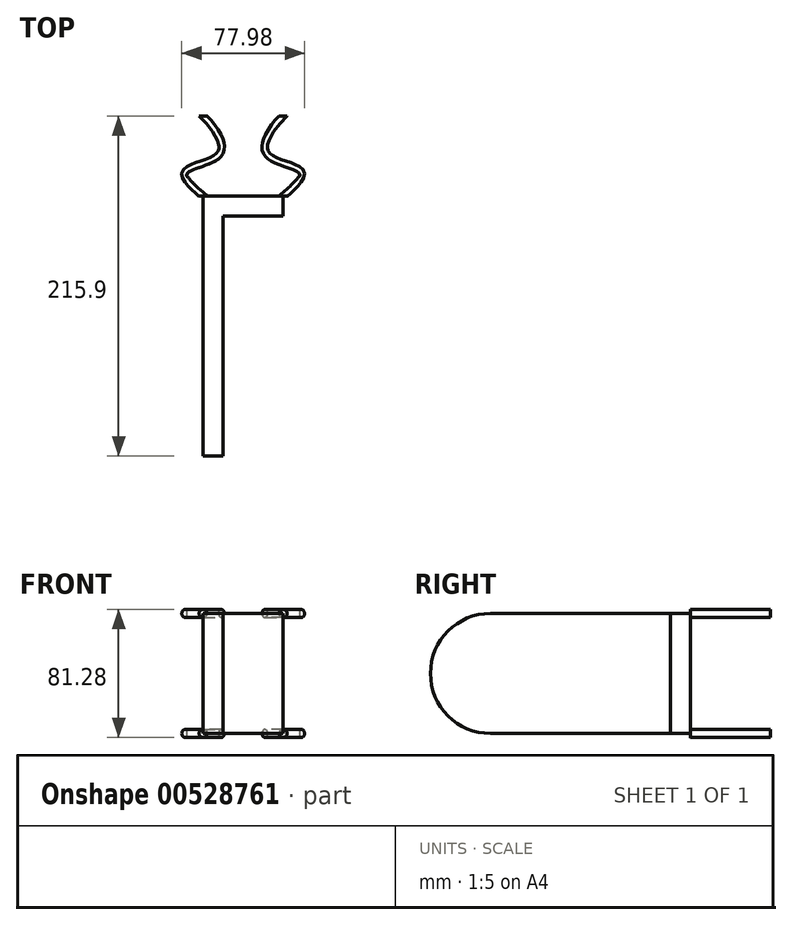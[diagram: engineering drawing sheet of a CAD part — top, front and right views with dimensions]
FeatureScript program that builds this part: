
annotation { "Feature Type Name" : "Feature", "Feature Type Description" : "" }
export const myFeature = defineFeature(function(context is Context, id is Id, definition is map)
    precondition{}
    {
        {
            var Q0;
            Q0=qCreatedBy(makeId("Front.planeOp"),FACE);
            var sketch = newSketch(context, id + "F0", { "sketchPlane" : qUnion([Q0])});
            skLineSegment(sketch, "E0.bottom", {"start": v(-50.8, 76.2) * mm, "end": v(0, 76.2) * mm});
            skLineSegment(sketch, "E0.top", {"start": v(-50.8, 0) * mm, "end": v(0, 0) * mm});
            skLineSegment(sketch, "E0.left", {"start": v(-50.8, 76.2) * mm, "end": v(-50.8, 0) * mm});
            skLineSegment(sketch, "E0.right", {"start": v(0, 76.2) * mm, "end": v(0, 0) * mm});
            skSolve(sketch);
        }
        {
            var Q0;
            Q0=makeQuery(id+"F0.imprint","IMPRINT",FACE,{"disambiguationData":[TD([[makeQuery(id+"F0.imprint","IMPRINT",EDGE,{"derivedFrom":sQuery(id+"F0.wireOp",EDGE,"E0.bottom")}),-1.0]])]});
            extrude(context, id + "F1", {"entities" : qUnion([Q0]), "depth" : 12.7 * mm, "offsetDistance" : 25.4 * mm});
        }
        {
            var Q0;
            Q0=qCreatedBy(makeId("Front.planeOp"),FACE);
            cPlane(context, id + "F2", {"entities" : qUnion([Q0]), "cplaneType" : CPlaneType.OFFSET, "offset" : 50.8 * mm, "oppositeDirection" : true, "width" : 152.4 * mm, "height" : 152.4 * mm});
        }
        {
            var Q0;
            Q0=qCreatedBy(id+"F2.planeOp",FACE);
            var sketch = newSketch(context, id + "F3", { "sketchPlane" : qUnion([Q0])});
            skCircle(sketch, "E1", {"center": v(0, 0) * mm, "radius": 2.54 * mm});
            skSolve(sketch);
        }
        {
            var Q0;
            Q0=makeQuery(id+"F1.opExtrude","SWEPT_FACE",FACE,{"disambiguationData":[OSD([sQuery(id+"F0.wireOp",EDGE,"E0.top")])]});
            var sketch = newSketch(context, id + "F4", { "sketchPlane" : qUnion([Q0])});
            skFitSpline(sketch, "E2", {"points": [v(0, 0) * mm, v(11.07, -15.46) * mm, v(-9.82, -26.33) * mm, v(0, -50.8) * mm], "startDerivative": vector(66.64, -57.68) * mm, "endDerivative": vector(75.5, -74.35) * mm});
            skSolve(sketch);
        }
        {
            var Q0;
            Q0=makeQuery(id+"F3.imprint","IMPRINT",FACE,{"disambiguationData":[TD([[makeQuery(id+"F3.imprint","IMPRINT",EDGE,{"derivedFrom":sQuery(id+"F3.wireOp",EDGE,"E1")}),1.0]])]});
            var Q1;
            Q1=sQuery(id+"F4.wireOp",EDGE,"E2");
            sweep(context, id + "F5", {"profiles" : qUnion([Q0]), "path" : qUnion([Q1])});
        }
        {
            var Q0;
            Q0=qCreatedBy(makeId("Right.planeOp"),FACE);
            cPlane(context, id + "F6", {"entities" : qUnion([Q0]), "cplaneType" : CPlaneType.OFFSET, "offset" : 25.4 * mm, "oppositeDirection" : true, "width" : 152.4 * mm, "height" : 152.4 * mm});
        }
        {
            var Q0;
            Q0=makeQuery(id+"F5.opSweep","SWEPT_BODY",BODY,{"disambiguationData":[OSD([sQuery(id+"F3.wireOp",EDGE,"E1"),sQuery(id+"F4.wireOp",EDGE,"E2")])]});
            var Q1;
            Q1=qCreatedBy(id+"F6.planeOp",FACE);
            mirror(context, id + "F7", {"entities" : qUnion([Q0]), "mirrorPlane" : qUnion([Q1])});
        }
        {
            var Q0;
            Q0=qCreatedBy(makeId("Top.planeOp"),FACE);
            cPlane(context, id + "F8", {"entities" : qUnion([Q0]), "cplaneType" : CPlaneType.OFFSET, "offset" : 38.1 * mm, "width" : 152.4 * mm, "height" : 152.4 * mm});
        }
        {
            var Q0;
            Q0=makeQuery(id+"F7.opPattern","COPY",BODY,{"derivedFrom":makeQuery(id+"F5.opSweep","SWEPT_BODY",BODY,{"disambiguationData":[OSD([sQuery(id+"F3.wireOp",EDGE,"E1"),sQuery(id+"F4.wireOp",EDGE,"E2")])]}),"instanceName":"1"});
            var Q1;
            Q1=makeQuery(id+"F5.opSweep","SWEPT_BODY",BODY,{"disambiguationData":[OSD([sQuery(id+"F3.wireOp",EDGE,"E1"),sQuery(id+"F4.wireOp",EDGE,"E2")])]});
            var Q2;
            Q2=qCreatedBy(id+"F8.planeOp",FACE);
            mirror(context, id + "F9", {"entities" : qUnion([Q0, Q1]), "mirrorPlane" : qUnion([Q2])});
        }
        {
            var Q0;
            Q0=makeQuery(id+"F1.opExtrude","SWEPT_FACE",FACE,{"disambiguationData":[OSD([sQuery(id+"F0.wireOp",EDGE,"E0.left")])]});
            var sketch = newSketch(context, id + "F10", { "sketchPlane" : qUnion([Q0])});
            skLineSegment(sketch, "E3.bottom", {"start": v(12.7, 0) * mm, "end": v(127, 0) * mm});
            skLineSegment(sketch, "E3.top", {"start": v(12.7, 76.2) * mm, "end": v(127, 76.2) * mm});
            skLineSegment(sketch, "E3.left", {"start": v(12.7, 0) * mm, "end": v(12.7, 76.2) * mm});
            skLineSegment(sketch, "E3.right", {"start": v(127, 0) * mm, "end": v(127, 76.2) * mm});
            skArc(sketch, "E4", {"start": v(127, 0) * mm, "mid": v(165.1, 38.1) * mm, "end": v(127, 76.2) * mm});
            skSolve(sketch);
        }
        {
            var Q0;
            Q0 = qSketchRegion(id + "F10", true);
            extrude(context, id + "F11", {"entities" : qUnion([Q0]), "operationType" : NewBodyOperationType.ADD, "oppositeDirection" : true, "depth" : 12.7 * mm, "offsetDistance" : 25.4 * mm});
        }
    });
